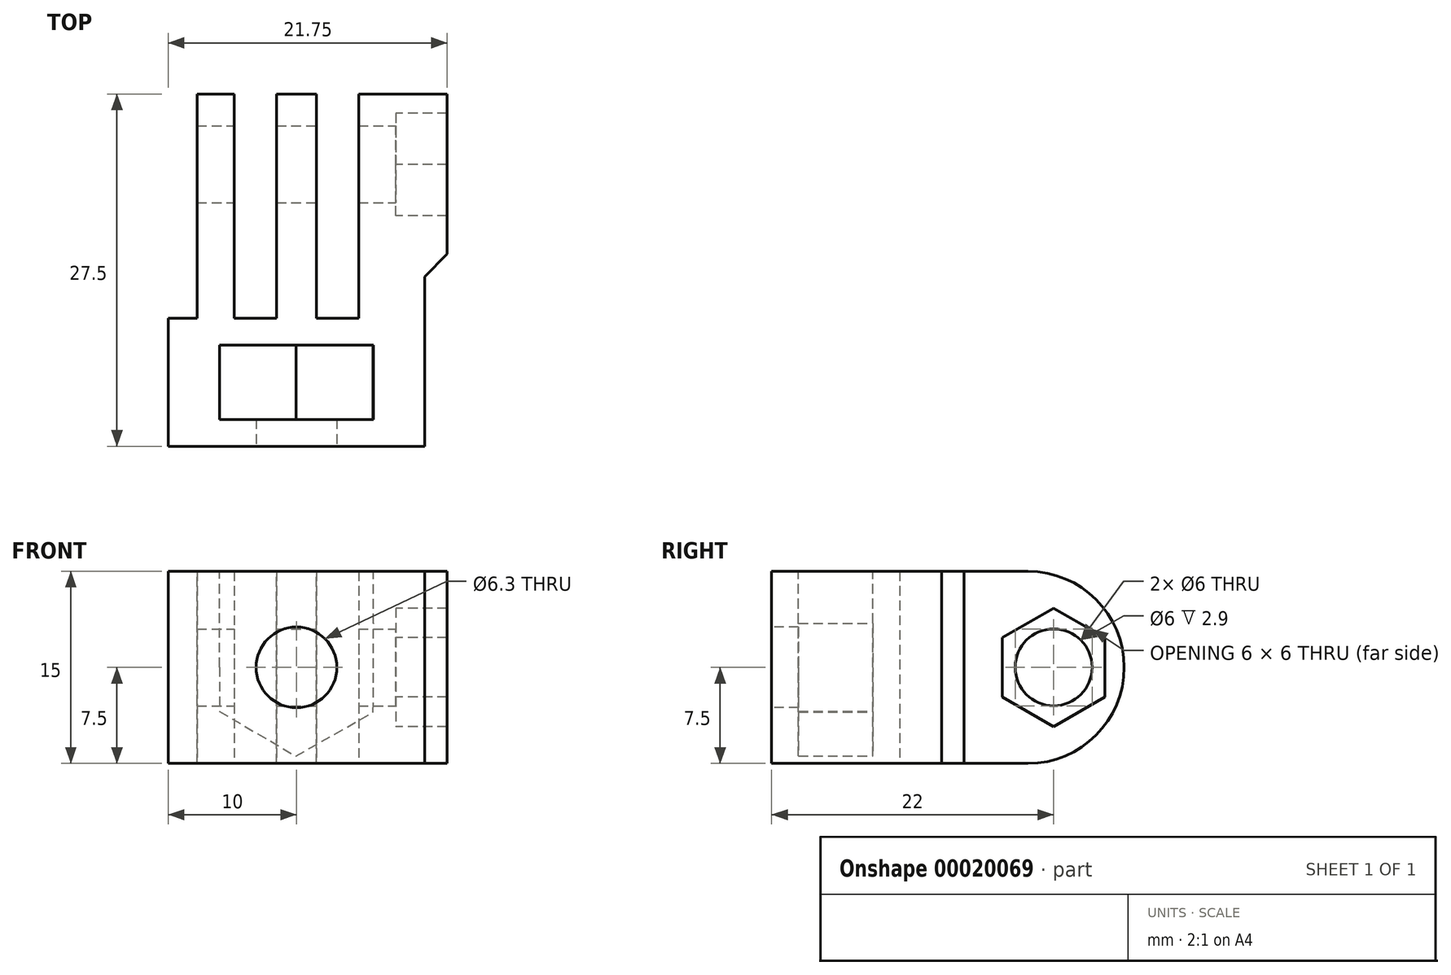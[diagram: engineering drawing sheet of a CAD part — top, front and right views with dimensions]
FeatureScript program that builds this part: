
annotation { "Feature Type Name" : "Feature", "Feature Type Description" : "" }
export const myFeature = defineFeature(function(context is Context, id is Id, definition is map)
    precondition{}
    {
        {
            var Q0;
            Q0=qCreatedBy(makeId("Top.planeOp"),FACE);
            var sketch = newSketch(context, id + "F0", { "sketchPlane" : qUnion([Q0])});
            skLineSegment(sketch, "E0.rect.bottom", {"start": v(10, 5) * mm, "end": v(-10, 5) * mm});
            skLineSegment(sketch, "E0.rect.top", {"start": v(10, -5) * mm, "end": v(-10, -5) * mm});
            skLineSegment(sketch, "E0.rect.left", {"start": v(10, 5) * mm, "end": v(10, -5) * mm});
            skLineSegment(sketch, "E0.rect.right", {"start": v(-10, 5) * mm, "end": v(-10, -5) * mm});
            skPoint(sketch, "E0.rect.middle", {"position": v(0, 0) * mm});
            skLineSegment(sketch, "E1", {"start": v(0, 5) * mm, "end": v(0, 22.5) * mm});
            skLineSegment(sketch, "E2", {"start": v(0, 22.5) * mm, "end": v(1.55, 22.5) * mm});
            skLineSegment(sketch, "E3", {"start": v(1.55, 22.5) * mm, "end": v(1.55, 5) * mm});
            skLineSegment(sketch, "E4", {"start": v(0, 22.5) * mm, "end": v(-1.55, 22.5) * mm});
            skLineSegment(sketch, "E5", {"start": v(-1.55, 22.5) * mm, "end": v(-1.55, 5) * mm});
            skLineSegment(sketch, "E6", {"start": v(-1.55, 5) * mm, "end": v(-4.85, 5) * mm});
            skLineSegment(sketch, "E7", {"start": v(-4.85, 5) * mm, "end": v(-4.85, 22.5) * mm});
            skLineSegment(sketch, "E8", {"start": v(-4.85, 22.5) * mm, "end": v(-7.75, 22.5) * mm});
            skLineSegment(sketch, "E9", {"start": v(-7.75, 22.5) * mm, "end": v(-7.75, 5) * mm});
            skLineSegment(sketch, "E10", {"start": v(1.55, 5) * mm, "end": v(4.85, 5) * mm});
            skLineSegment(sketch, "E11", {"start": v(4.85, 5) * mm, "end": v(4.85, 22.5) * mm});
            skLineSegment(sketch, "E12", {"start": v(4.85, 22.5) * mm, "end": v(7.75, 22.5) * mm});
            skLineSegment(sketch, "E13", {"start": v(7.75, 22.5) * mm, "end": v(7.75, 5) * mm});
            skLineSegment(sketch, "E14", {"start": v(10, 5) * mm, "end": v(7.75, 5) * mm});
            skSolve(sketch);
        }
        {
            var Q0;
            Q0=makeQuery(id+"F0.imprint","IMPRINT",FACE,{"disambiguationData":[TD([[makeQuery(id+"F0.imprint","IMPRINT",EDGE,{"derivedFrom":sQuery(id+"F0.wireOp",EDGE,"E0.rect.bottom")}),1.0]])]});
            var Q1;
            {var subQ1=sQuery(id+"F0.wireOp",EDGE,"E11");Q1=makeQuery(id+"F0.imprint","IMPRINT",FACE,{"disambiguationData":[TD([[makeQuery(id+"F0.imprint","IMPRINT",EDGE,{"derivedFrom":subQ1}),-1.0]])]});}
            var Q2;
            {var subQ1=sQuery(id+"F0.wireOp",EDGE,"E1");Q2=makeQuery(id+"F0.imprint","IMPRINT",FACE,{"disambiguationData":[TD([[makeQuery(id+"F0.imprint","IMPRINT",EDGE,{"derivedFrom":subQ1}),-1.0]])]});}
            var Q3;
            {var subQ1=sQuery(id+"F0.wireOp",EDGE,"E1");Q3=makeQuery(id+"F0.imprint","IMPRINT",FACE,{"disambiguationData":[TD([[makeQuery(id+"F0.imprint","IMPRINT",EDGE,{"derivedFrom":subQ1}),1.0]])]});}
            var Q4;
            {var subQ1=sQuery(id+"F0.wireOp",EDGE,"E7");Q4=makeQuery(id+"F0.imprint","IMPRINT",FACE,{"disambiguationData":[TD([[makeQuery(id+"F0.imprint","IMPRINT",EDGE,{"derivedFrom":subQ1}),1.0]])]});}
            extrude(context, id + "F1", {"entities" : qUnion([Q0, Q1, Q2, Q3, Q4]), "depth" : 15 * mm});
        }
        {
            var Q0;
            Q0=makeQuery(id+"F1.opExtrude","SWEPT_FACE",FACE,{"disambiguationData":[OSD([sQuery(id+"F0.wireOp",EDGE,"E13")])]});
            var sketch = newSketch(context, id + "F2", { "sketchPlane" : qUnion([Q0])});
            skLineSegment(sketch, "E15", {"start": v(22.5, 7.5) * mm, "end": v(17, 7.5) * mm});
            skCircle(sketch, "E16", {"center": v(17, 7.5) * mm, "radius": 3 * mm});
            skSolve(sketch);
        }
        {
            var Q0;
            Q0=makeQuery(id+"F2.imprint","IMPRINT",FACE,{"disambiguationData":[TD([[makeQuery(id+"F2.imprint","IMPRINT",EDGE,{"derivedFrom":sQuery(id+"F2.wireOp",EDGE,"E16")}),1.0]])]});
            extrude(context, id + "F3", {"entities" : qUnion([Q0]), "operationType" : NewBodyOperationType.REMOVE, "endBound" : BoundingType.THROUGH_ALL, "oppositeDirection" : true, "depth" : 25 * mm});
        }
        {
            var Q0;
            Q0=makeQuery(id+"F1.opExtrude","CAP_EDGE",EDGE,{"disambiguationData":[OSD([sQuery(id+"F0.wireOp",EDGE,"E12")])],"isStart":false});
            var Q1;
            Q1=makeQuery(id+"F1.opExtrude","CAP_EDGE",EDGE,{"disambiguationData":[OSD([sQuery(id+"F0.wireOp",EDGE,"E12")])],"isStart":true});
            var Q2;
            Q2=makeQuery(id+"F1.opExtrude","CAP_EDGE",EDGE,{"disambiguationData":[OSD([sQuery(id+"F0.wireOp",EDGE,"E2"),sQuery(id+"F0.wireOp",EDGE,"E4")])],"isStart":false});
            var Q3;
            Q3=makeQuery(id+"F1.opExtrude","CAP_EDGE",EDGE,{"disambiguationData":[OSD([sQuery(id+"F0.wireOp",EDGE,"E2"),sQuery(id+"F0.wireOp",EDGE,"E4")])],"isStart":true});
            var Q4;
            Q4=makeQuery(id+"F1.opExtrude","CAP_EDGE",EDGE,{"disambiguationData":[OSD([sQuery(id+"F0.wireOp",EDGE,"E8")])],"isStart":false});
            var Q5;
            Q5=makeQuery(id+"F1.opExtrude","CAP_EDGE",EDGE,{"disambiguationData":[OSD([sQuery(id+"F0.wireOp",EDGE,"E8")])],"isStart":true});
            fillet(context, id + "F4", {"entities" : qUnion([Q0, Q1, Q2, Q3, Q4, Q5]), "radius" : 7.5 * mm, "tangentPropagation" : true, "allowEdgeOverflow" : false});
        }
        {
            var Q0;
            Q0=makeQuery(id+"F1.opExtrude","SWEPT_FACE",FACE,{"disambiguationData":[OSD([sQuery(id+"F0.wireOp",EDGE,"E13")])]});
            var sketch = newSketch(context, id + "F5", { "sketchPlane" : qUnion([Q0])});
            skCircle(sketch, "E17.cCircle", {"center": v(17, 7.5) * mm, "radius": 4 * mm, "construction": true});
            skLineSegment(sketch, "E17.0", {"start": v(21, 9.8) * mm, "end": v(21, 5.2) * mm});
            skLineSegment(sketch, "E17.1", {"start": v(21, 5.2) * mm, "end": v(17, 2.88) * mm});
            skLineSegment(sketch, "E17.2", {"start": v(17, 2.88) * mm, "end": v(13, 5.2) * mm});
            skLineSegment(sketch, "E17.3", {"start": v(13, 5.2) * mm, "end": v(13, 9.8) * mm});
            skLineSegment(sketch, "E17.4", {"start": v(13, 9.8) * mm, "end": v(17, 12.12) * mm});
            skLineSegment(sketch, "E17.5", {"start": v(17, 12.12) * mm, "end": v(21, 9.8) * mm});
            skPoint(sketch, "E17.0.midPoint", {"position": v(21, 7.5) * mm});
            skLineSegment(sketch, "E18", {"start": v(17, 7.5) * mm, "end": v(21, 7.5) * mm});
            skSolve(sketch);
        }
        {
            var Q0;
            {var subQ2=sQuery(id+"F5.wireOp",EDGE,"E17.1");Q0=makeQuery(id+"F5.imprint","IMPRINT",FACE,{"disambiguationData":[TD([[makeQuery(id+"F5.imprint","IMPRINT",EDGE,{"derivedFrom":subQ2}),1.0]])]});}
            extrude(context, id + "F6", {"entities" : qUnion([Q0]), "operationType" : NewBodyOperationType.ADD, "depth" : 4 * mm});
        }
        {
            var Q0;
            Q0=makeQuery(id+"F6.opExtrude","CAP_EDGE",EDGE,{"disambiguationData":[OSD([sQuery(id+"F0.wireOp",EDGE,"E0.rect.bottom"),sQuery(id+"F0.wireOp",EDGE,"E13"),sQuery(id+"F0.wireOp",EDGE,"E14")])],"isStart":false});
            chamfer(context, id + "F7", {"entities" : qUnion([Q0]), "width" : 5 * mm, "tangentPropagation" : true});
        }
        {
            var Q0;
            Q0=makeQuery(id+"F1.opExtrude","SWEPT_FACE",FACE,{"disambiguationData":[OSD([sQuery(id+"F0.wireOp",EDGE,"E0.rect.top")])]});
            var sketch = newSketch(context, id + "F8", { "sketchPlane" : qUnion([Q0])});
            skLineSegment(sketch, "E19", {"start": v(-10, 7.5) * mm, "end": v(0, 7.5) * mm});
            skCircle(sketch, "E20", {"center": v(0, 7.5) * mm, "radius": 3.15 * mm});
            skSolve(sketch);
        }
        {
            var Q0;
            Q0=makeQuery(id+"F8.imprint","IMPRINT",FACE,{"disambiguationData":[TD([[makeQuery(id+"F8.imprint","IMPRINT",EDGE,{"derivedFrom":sQuery(id+"F8.wireOp",EDGE,"E20")}),1.0]])]});
            extrude(context, id + "F9", {"entities" : qUnion([Q0]), "operationType" : NewBodyOperationType.REMOVE, "oppositeDirection" : true, "depth" : 7.8 * mm});
        }
        {
            var Q0;
            {var subQ0=sQuery(id+"F0.wireOp",EDGE,"E13");Q0=makeQuery(id+"F6.boolean.opBoolean","MERGE",FACE,{"derivedFrom":[makeQuery(id+"F1.opExtrude","CAP_FACE",FACE,{"disambiguationData":[OSD([sQuery(id+"F0.wireOp",EDGE,"E0.rect.bottom"),sQuery(id+"F0.wireOp",EDGE,"E0.rect.top"),sQuery(id+"F0.wireOp",EDGE,"E0.rect.left"),sQuery(id+"F0.wireOp",EDGE,"E0.rect.right"),sQuery(id+"F0.wireOp",EDGE,"E2"),sQuery(id+"F0.wireOp",EDGE,"E3"),sQuery(id+"F0.wireOp",EDGE,"E4"),sQuery(id+"F0.wireOp",EDGE,"E5"),sQuery(id+"F0.wireOp",EDGE,"E6"),sQuery(id+"F0.wireOp",EDGE,"E7"),sQuery(id+"F0.wireOp",EDGE,"E8"),sQuery(id+"F0.wireOp",EDGE,"E9"),sQuery(id+"F0.wireOp",EDGE,"E10"),sQuery(id+"F0.wireOp",EDGE,"E11"),sQuery(id+"F0.wireOp",EDGE,"E12"),subQ0,sQuery(id+"F0.wireOp",EDGE,"E14")])],"isStart":false}),makeQuery(id+"F6.opExtrude","SWEPT_FACE",FACE,{"disambiguationData":[OSD([subQ0]),TDD([makeQuery(id+"F5.imprint","IMPRINT",EDGE,{"derivedFrom":makeQuery(id+"F1.opExtrude","CAP_EDGE",EDGE,{"disambiguationData":[OSD([subQ0])],"isStart":false})})])]})]});}
            var sketch = newSketch(context, id + "F10", { "sketchPlane" : qUnion([Q0])});
            skLineSegment(sketch, "E21.rect.bottom", {"start": v(6, -2.9) * mm, "end": v(-6, -2.9) * mm});
            skLineSegment(sketch, "E21.rect.top", {"start": v(6, 2.9) * mm, "end": v(-6, 2.9) * mm});
            skLineSegment(sketch, "E21.rect.left", {"start": v(6, -2.9) * mm, "end": v(6, 2.9) * mm});
            skLineSegment(sketch, "E21.rect.right", {"start": v(-6, -2.9) * mm, "end": v(-6, 2.9) * mm});
            skPoint(sketch, "E21.rect.middle", {"position": v(0, 0) * mm});
            skLineSegment(sketch, "E22", {"start": v(6, -2.9) * mm, "end": v(10, -2.9) * mm});
            skLineSegment(sketch, "E23", {"start": v(6, -2.9) * mm, "end": v(6, -5) * mm});
            skSolve(sketch);
        }
        {
            var Q0;
            Q0=makeQuery(id+"F10.imprint","IMPRINT",FACE,{"disambiguationData":[TD([[makeQuery(id+"F10.imprint","IMPRINT",EDGE,{"derivedFrom":sQuery(id+"F10.wireOp",EDGE,"E21.rect.bottom")}),-1.0]])]});
            extrude(context, id + "F11", {"entities" : qUnion([Q0]), "operationType" : NewBodyOperationType.REMOVE, "oppositeDirection" : true, "depth" : 7.5 * mm});
        }
        {
            var Q0;
            Q0=makeQuery(id+"F11.boolean.opBoolean","COPY",FACE,{"derivedFrom":makeQuery(id+"F11.opExtrude","SWEPT_FACE",FACE,{"disambiguationData":[OSD([sQuery(id+"F10.wireOp",EDGE,"E21.rect.top")])]})});
            var sketch = newSketch(context, id + "F12", { "sketchPlane" : qUnion([Q0])});
            skCircle(sketch, "E24.cCircle", {"center": v(0, 7.5) * mm, "radius": 6 * mm, "construction": true});
            skLineSegment(sketch, "E24.0", {"start": v(0.04, 14.43) * mm, "end": v(6.02, 10.93) * mm});
            skLineSegment(sketch, "E24.1", {"start": v(6.02, 10.93) * mm, "end": v(5.98, 4) * mm});
            skLineSegment(sketch, "E24.2", {"start": v(5.98, 4) * mm, "end": v(-0.04, 0.57) * mm});
            skLineSegment(sketch, "E24.3", {"start": v(-0.04, 0.57) * mm, "end": v(-6.02, 4.07) * mm});
            skLineSegment(sketch, "E24.4", {"start": v(-6.02, 4.07) * mm, "end": v(-5.98, 11) * mm});
            skLineSegment(sketch, "E24.5", {"start": v(-5.98, 11) * mm, "end": v(0.04, 14.43) * mm});
            skPoint(sketch, "E24.0.midPoint", {"position": v(3.03, 12.68) * mm});
            skLineSegment(sketch, "E25", {"start": v(0, 7.5) * mm, "end": v(3.03, 12.68) * mm});
            skSolve(sketch);
        }
        {
            var Q0;
            {var subQ1=sQuery(id+"F12.wireOp",EDGE,"E24.1");Q0=makeQuery(id+"F12.imprint","IMPRINT",FACE,{"disambiguationData":[TD([[makeQuery(id+"F12.imprint","IMPRINT",EDGE,{"derivedFrom":subQ1}),-1.0]])]});}
            var Q1;
            Q1=makeQuery(id+"F11.boolean.opBoolean","COPY",FACE,{"derivedFrom":makeQuery(id+"F11.opExtrude","SWEPT_FACE",FACE,{"disambiguationData":[OSD([sQuery(id+"F10.wireOp",EDGE,"E21.rect.bottom")])]})});
            extrude(context, id + "F13", {"entities" : qUnion([Q0]), "operationType" : NewBodyOperationType.REMOVE, "endBound" : BoundingType.UP_TO_SURFACE, "endBoundEntityFace" : qUnion([Q1]), "depth" : 25 * mm});
        }
    });
